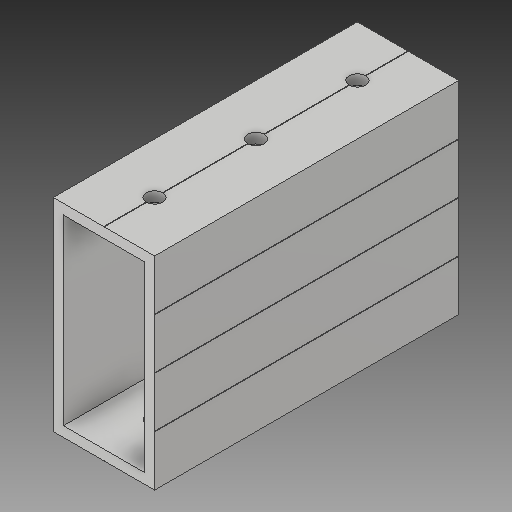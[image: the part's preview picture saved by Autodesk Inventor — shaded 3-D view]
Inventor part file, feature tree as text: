
AUTODESK INVENTOR PART (.ipt)
format: ipt  version: 2017 (Build 210142000, 142)  size: 203,776 bytes
history: native  units: in
note: dims shown in document units (in); Inventor stores cm internally (conversion verified against a paired STEP export)
features: other x3, sketch x2
ambient origin geometry x8: Origin, YZ Plane, XZ Plane, XY Plane, X Axis, Y Axis, Z Axis, Center Point
bodies: Solid1 (feature_tree)
feature tree (5):
  other  "SideBlock.ipt"
  other  "Solid1::SideBlock.ipt"
  other  "TaggingFeature1"
  sketch  "Sketch1"  dims[d0=0.3937in]
  sketch  "Sketch2"
